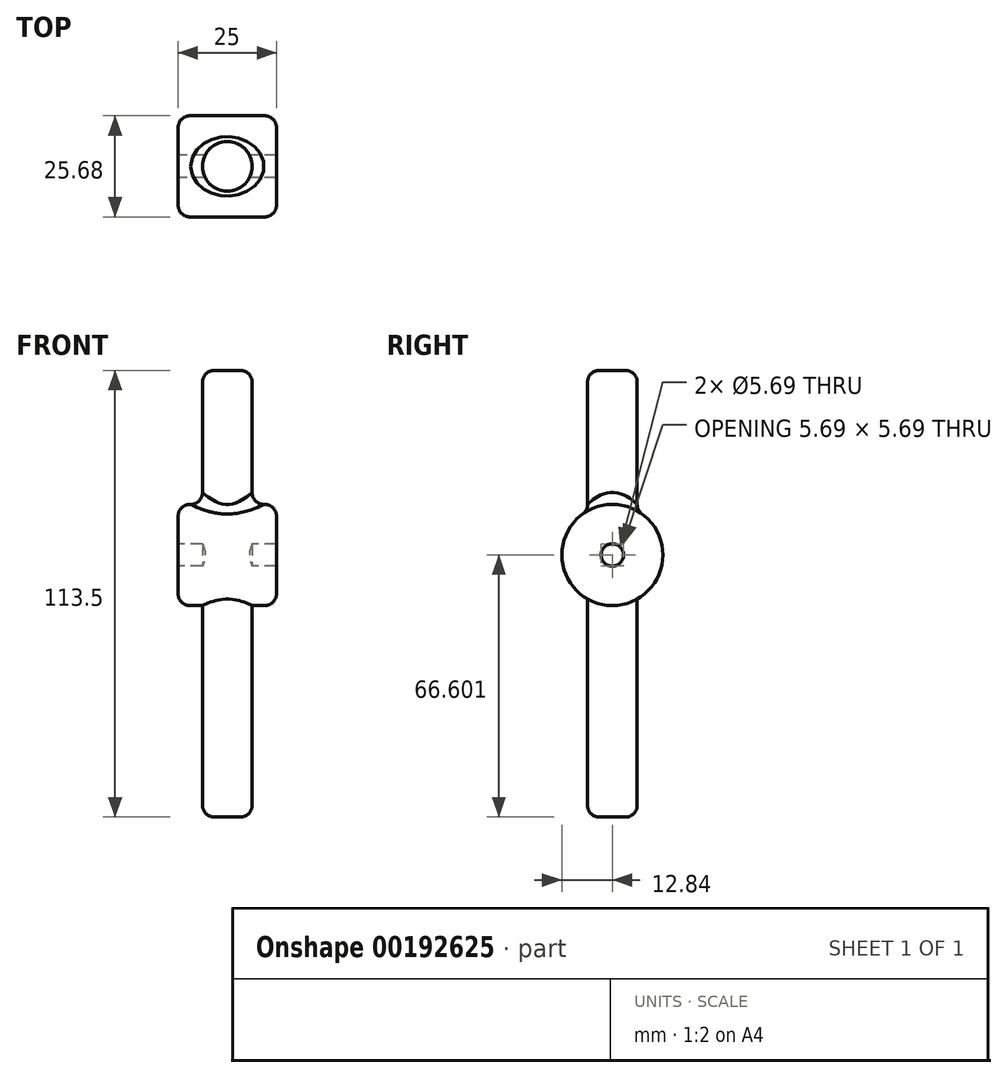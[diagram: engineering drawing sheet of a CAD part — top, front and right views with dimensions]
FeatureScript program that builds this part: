
annotation { "Feature Type Name" : "Feature", "Feature Type Description" : "" }
export const myFeature = defineFeature(function(context is Context, id is Id, definition is map)
    precondition{}
    {
        {
            var Q0;
            Q0=qCreatedBy(makeId("Top.planeOp"),FACE);
            var sketch = newSketch(context, id + "F0", { "sketchPlane" : qUnion([Q0])});
            skCircle(sketch, "E0", {"center": v(0, 0) * mm, "radius": 6.3 * mm});
            skSolve(sketch);
        }
        {
            var Q0;
            Q0 = qSketchRegion(id + "F0", true);
            extrude(context, id + "F1", {"entities" : qUnion([Q0]), "depth" : 113.5 * mm, "offsetDistance" : 25 * mm});
        }
        {
            var Q0;
            Q0=qCreatedBy(makeId("Right.planeOp"),FACE);
            var sketch = newSketch(context, id + "F2", { "sketchPlane" : qUnion([Q0])});
            skCircle(sketch, "E1", {"center": v(0, 66.6) * mm, "radius": 12.84 * mm});
            skCircle(sketch, "E2", {"center": v(0, 66.6) * mm, "radius": 2.85 * mm});
            skSolve(sketch);
        }
        {
            var Q0;
            Q0 = qSketchRegion(id + "F2", true);
            extrude(context, id + "F3", {"entities" : qUnion([Q0]), "operationType" : NewBodyOperationType.ADD, "endBound" : BoundingType.SYMMETRIC, "depth" : 25 * mm, "offsetDistance" : 25 * mm});
        }
        {
            var Q0;
            Q0=makeQuery(id+"F3.opExtrude","CAP_EDGE",EDGE,{"disambiguationData":[OSD([sQuery(id+"F2.wireOp",EDGE,"E1")])],"isStart":false});
            var Q1;
            Q1=makeQuery(id+"F3.opExtrude","CAP_EDGE",EDGE,{"disambiguationData":[OSD([sQuery(id+"F2.wireOp",EDGE,"E1")])],"isStart":true});
            var Q2;
            Q2=makeQuery(id+"F3.boolean.opBoolean","INTERSECT",EDGE,{"disambiguationData":[OD(1.0)],"derivedFrom":[makeQuery(id+"F1.opExtrude","SWEPT_FACE",FACE,{"disambiguationData":[OSD([sQuery(id+"F0.wireOp",EDGE,"E0")])]}),makeQuery(id+"F3.opExtrude","SWEPT_FACE",FACE,{"disambiguationData":[OSD([sQuery(id+"F2.wireOp",EDGE,"E1")])]})]});
            var Q3;
            Q3=makeQuery(id+"F1.opExtrude","CAP_EDGE",EDGE,{"disambiguationData":[OSD([sQuery(id+"F0.wireOp",EDGE,"E0")])],"isStart":false});
            var Q4;
            Q4=makeQuery(id+"F1.opExtrude","CAP_EDGE",EDGE,{"disambiguationData":[OSD([sQuery(id+"F0.wireOp",EDGE,"E0")])],"isStart":true});
            fillet(context, id + "F4", {"entities" : qUnion([Q0, Q1, Q2, Q3, Q4]), "radius" : 3 * mm, "tangentPropagation" : true, "allowEdgeOverflow" : false});
        }
    });
